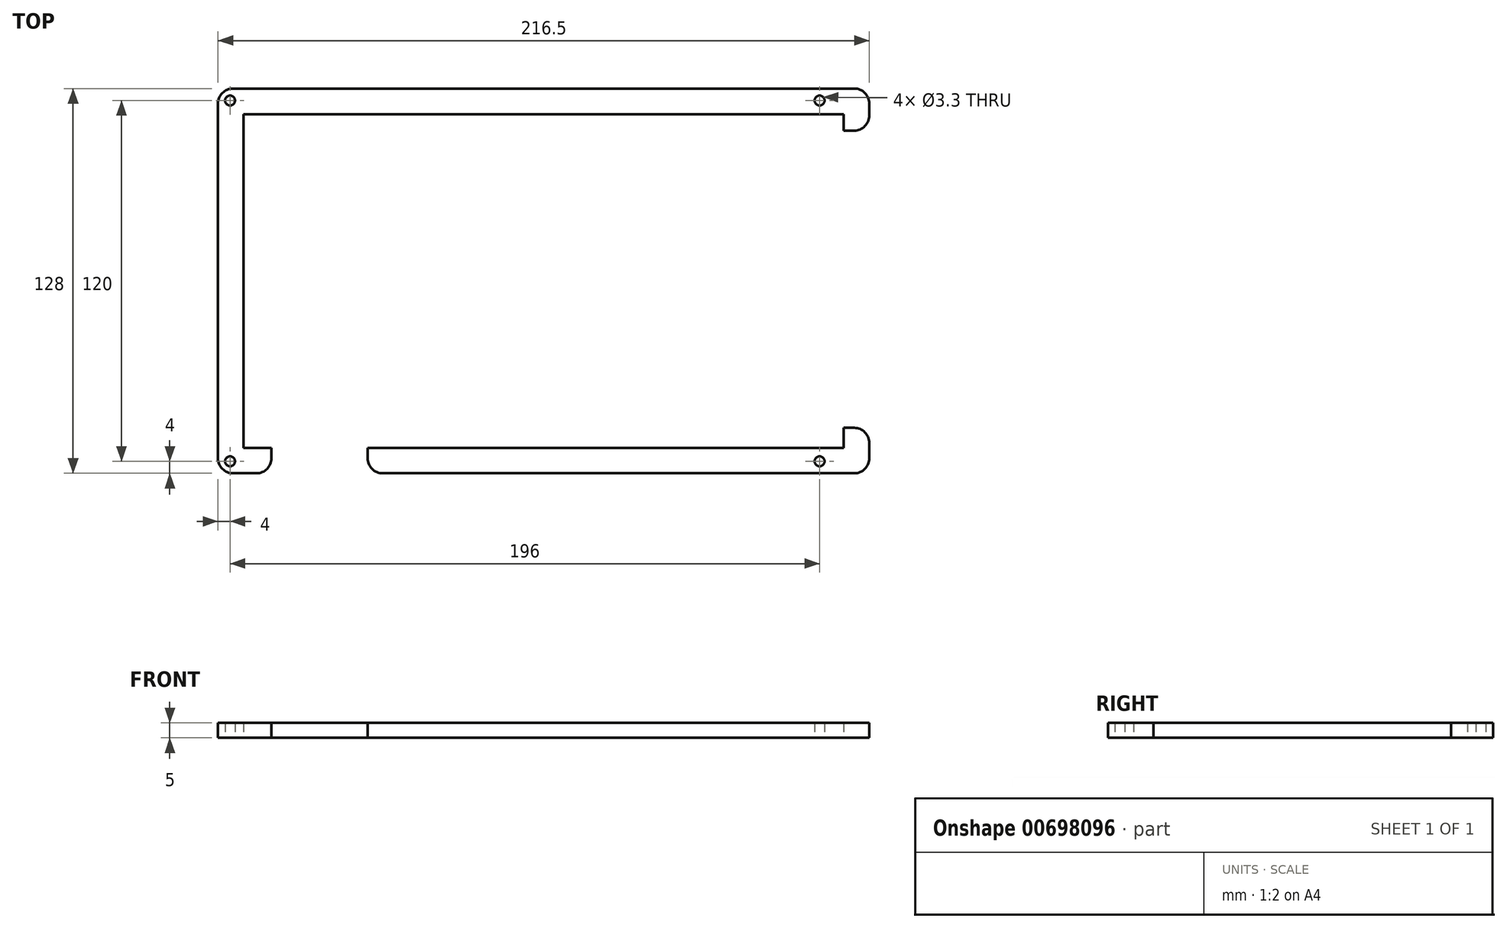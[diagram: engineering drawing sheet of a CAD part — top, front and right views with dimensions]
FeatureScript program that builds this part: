
annotation { "Feature Type Name" : "Feature", "Feature Type Description" : "" }
export const myFeature = defineFeature(function(context is Context, id is Id, definition is map)
    precondition{}
    {
        {
            var Q0;
            Q0=qCreatedBy(makeId("Top.planeOp"),FACE);
            var sketch = newSketch(context, id + "F0", { "sketchPlane" : qUnion([Q0])});
            skLineSegment(sketch, "E0.bottom", {"start": v(83, 50.5) * mm, "end": v(-57.08, 50.5) * mm});
            skLineSegment(sketch, "E0.top", {"start": v(83, -50.5) * mm, "end": v(-83, -50.5) * mm});
            skLineSegment(sketch, "E0.left", {"start": v(83, 50.5) * mm, "end": v(83, -50.5) * mm});
            skLineSegment(sketch, "E0.right", {"start": v(-83, 50.5) * mm, "end": v(-83, -50.5) * mm});
            skPoint(sketch, "E0.middle", {"position": v(0, 0) * mm});
            skLineSegment(sketch, "E1.0", {"start": v(-91, 54.5) * mm, "end": v(-91, -53.5) * mm, "construction": true});
            skLineSegment(sketch, "E1.1", {"start": v(93, 54.5) * mm, "end": v(-91, 54.5) * mm, "construction": true});
            skLineSegment(sketch, "E1.2", {"start": v(93, 54.5) * mm, "end": v(93, -53.5) * mm, "construction": true});
            skLineSegment(sketch, "E1.3", {"start": v(93, -53.5) * mm, "end": v(-91, -53.5) * mm, "construction": true});
            skLineSegment(sketch, "E2.0", {"start": v(103, 64.5) * mm, "end": v(-57.08, 64.5) * mm});
            skLineSegment(sketch, "E2.2", {"start": v(103, -63.5) * mm, "end": v(-57.08, -63.5) * mm});
            skLineSegment(sketch, "E2.3", {"start": v(-101, 64.5) * mm, "end": v(-101, -63.5) * mm});
            skLineSegment(sketch, "E3.0", {"start": v(99, 60.5) * mm, "end": v(-97, 60.5) * mm, "construction": true});
            skLineSegment(sketch, "E3.1", {"start": v(99, 60.5) * mm, "end": v(99, -59.5) * mm, "construction": true});
            skLineSegment(sketch, "E3.2", {"start": v(99, -59.5) * mm, "end": v(-97, -59.5) * mm, "construction": true});
            skLineSegment(sketch, "E3.3", {"start": v(-97, 60.5) * mm, "end": v(-97, -59.5) * mm, "construction": true});
            skLineSegment(sketch, "E4", {"start": v(103, 64.5) * mm, "end": v(115.5, 64.5) * mm});
            skLineSegment(sketch, "E5", {"start": v(115.5, -63.5) * mm, "end": v(103, -63.5) * mm});
            skLineSegment(sketch, "E6", {"start": v(115.5, 64.5) * mm, "end": v(115.5, 50.5) * mm});
            skPoint(sketch, "E7.orphan", {"position": v(133, -63.5) * mm});
            skLineSegment(sketch, "E8.0", {"start": v(103, 56) * mm, "end": v(107, 56) * mm});
            skLineSegment(sketch, "E8.1", {"start": v(-92.5, 56) * mm, "end": v(-92.5, -55) * mm});
            skLineSegment(sketch, "E8.2", {"start": v(103, -55) * mm, "end": v(-57.08, -55) * mm});
            skLineSegment(sketch, "E8.3", {"start": v(103, 56) * mm, "end": v(-57.08, 56) * mm});
            skLineSegment(sketch, "E8.4", {"start": v(107, -55) * mm, "end": v(103, -55) * mm});
            skLineSegment(sketch, "E8.5", {"start": v(107, 56) * mm, "end": v(107, 50.5) * mm});
            skLineSegment(sketch, "E9", {"start": v(-83.1, 56) * mm, "end": v(-83.07, 54.5) * mm});
            skLineSegment(sketch, "E10.trimOffspring", {"start": v(-83.24, 64.5) * mm, "end": v(-101, 64.5) * mm});
            skLineSegment(sketch, "E11.trimOffspring", {"start": v(-83.1, 56) * mm, "end": v(-92.5, 56) * mm});
            skLineSegment(sketch, "E12", {"start": v(-83.24, -63.5) * mm, "end": v(-83.24, -55) * mm});
            skLineSegment(sketch, "E13.trimOffspring", {"start": v(-57.08, 56) * mm, "end": v(-57.08, 54.5) * mm});
            skLineSegment(sketch, "E14", {"start": v(-83.24, 64.5) * mm, "end": v(-57.08, 64.5) * mm});
            skLineSegment(sketch, "E15", {"start": v(-57.08, 56) * mm, "end": v(-83.1, 56) * mm});
            skLineSegment(sketch, "E16.trimOffspring", {"start": v(-83.24, -55) * mm, "end": v(-92.5, -55) * mm});
            skLineSegment(sketch, "E17.trimOffspring", {"start": v(-83.24, -63.5) * mm, "end": v(-101, -63.5) * mm});
            skLineSegment(sketch, "E18.trimOffspring", {"start": v(-57.08, -55) * mm, "end": v(-57.08, -53.5) * mm});
            skLineSegment(sketch, "E19", {"start": v(-51.24, -63.5) * mm, "end": v(-51.24, -55) * mm});
            skLineSegment(sketch, "E20", {"start": v(107, 50.5) * mm, "end": v(115.5, 50.5) * mm});
            skLineSegment(sketch, "E21", {"start": v(107, -48.38) * mm, "end": v(115.5, -48.38) * mm});
            skLineSegment(sketch, "E22.trimOffspring", {"start": v(107, -48.38) * mm, "end": v(107, -55) * mm});
            skLineSegment(sketch, "E23.trimOffspring", {"start": v(115.5, -48.38) * mm, "end": v(115.5, -63.5) * mm});
            skSolve(sketch);
        }
        {
            var Q0;
            Q0=makeQuery(id+"F0.imprint","IMPRINT",FACE,{"disambiguationData":[TD([[makeQuery(id+"F0.imprint","IMPRINT",EDGE,{"derivedFrom":sQuery(id+"F0.wireOp",EDGE,"E2.0")}),1.0]])]});
            var Q1;
            Q1=makeQuery(id+"F0.imprint","IMPRINT",FACE,{"disambiguationData":[TD([[makeQuery(id+"F0.imprint","IMPRINT",EDGE,{"derivedFrom":sQuery(id+"F0.wireOp",EDGE,"E0.bottom")}),-1.0]])]});
            var Q2;
            {var subQ3=sQuery(id+"F0.wireOp",EDGE,"E5");Q2=makeQuery(id+"F0.imprint","IMPRINT",FACE,{"disambiguationData":[TD([[makeQuery(id+"F0.imprint","IMPRINT",EDGE,{"derivedFrom":subQ3}),-1.0]])]});}
            extrude(context, id + "F1", {"entities" : qUnion([Q0, Q1, Q2]), "depth" : 5 * mm, "offsetDistance" : 25 * mm});
        }
        {
            var Q0;
            Q0=sQuery(id+"F0.wireOp",VERTEX,"E3.0.end");
            var Q1;
            Q1=sQuery(id+"F0.wireOp",VERTEX,"E3.0.start");
            var Q2;
            Q2=sQuery(id+"F0.wireOp",VERTEX,"E3.2.end");
            var Q3;
            Q3=sQuery(id+"F0.wireOp",VERTEX,"E3.1.end");
            var Q4;
            Q4=makeQuery(id+"F1.opExtrude","SWEPT_BODY",BODY,{"disambiguationData":[OSD([sQuery(id+"F0.wireOp",EDGE,"E0.bottom"),sQuery(id+"F0.wireOp",EDGE,"E0.top"),sQuery(id+"F0.wireOp",EDGE,"E0.left"),sQuery(id+"F0.wireOp",EDGE,"E0.right"),sQuery(id+"F0.wireOp",EDGE,"E2.0"),sQuery(id+"F0.wireOp",EDGE,"E2.1"),sQuery(id+"F0.wireOp",EDGE,"E2.2"),sQuery(id+"F0.wireOp",EDGE,"E2.3")])]});
            var Q5;
            Q5=makeQuery(id+"F1.opExtrude","SWEPT_BODY",BODY,{"disambiguationData":[OSD([sQuery(id+"F0.wireOp",EDGE,"E2.2"),sQuery(id+"F0.wireOp",EDGE,"E5"),sQuery(id+"F0.wireOp",EDGE,"E8.2"),sQuery(id+"F0.wireOp",EDGE,"E8.4"),sQuery(id+"F0.wireOp",EDGE,"E19"),sQuery(id+"F0.wireOp",EDGE,"E21"),sQuery(id+"F0.wireOp",EDGE,"E22.trimOffspring"),sQuery(id+"F0.wireOp",EDGE,"E23.trimOffspring")])]});
            hole(context, id + "F2", {"style" : HoleStyle.SIMPLE, "endStyle" : HoleEndStyle.THROUGH, "oppositeDirection" : true, "standardTappedOrClearance" : lookupTablePath({ "standard" : "ISO", "fit" : "Normal", "size" : "M3", "type" : "Clearance" }), "standardBlindInLast" : lookupTablePath({ "fit" : "Standard", "standard" : "ISO", "size" : "M3", "type" : "Clearance" }), "holeDiameter" : 3.3 * mm, "majorDiameter" : 5 * mm, "isTappedThrough" : true, "tappedDepth" : 12 * mm, "tapClearance" : 3, "startFromSketch" : true, "locations" : qUnion([Q0, Q1, Q2, Q3]), "scope" : qUnion([Q4, Q5])});
        }
        {
            var Q0;
            Q0=makeQuery(id+"F1.opExtrude","SWEPT_EDGE",EDGE,{"disambiguationData":[OSD([sQuery(id+"F0.wireOp",EDGE,"E2.3"),sQuery(id+"F0.wireOp",EDGE,"E10.trimOffspring")])]});
            var Q1;
            Q1=makeQuery(id+"F1.opExtrude","SWEPT_EDGE",EDGE,{"disambiguationData":[OSD([sQuery(id+"F0.wireOp",EDGE,"E4"),sQuery(id+"F0.wireOp",EDGE,"E6")])]});
            var Q2;
            Q2=makeQuery(id+"F1.opExtrude","SWEPT_EDGE",EDGE,{"disambiguationData":[OSD([sQuery(id+"F0.wireOp",EDGE,"E5"),sQuery(id+"F0.wireOp",EDGE,"E6")])]});
            var Q3;
            Q3=makeQuery(id+"F1.opExtrude","SWEPT_EDGE",EDGE,{"disambiguationData":[OSD([sQuery(id+"F0.wireOp",EDGE,"E2.2"),sQuery(id+"F0.wireOp",EDGE,"E19")])]});
            var Q4;
            Q4=makeQuery(id+"F1.opExtrude","SWEPT_EDGE",EDGE,{"disambiguationData":[OSD([sQuery(id+"F0.wireOp",EDGE,"E2.3"),sQuery(id+"F0.wireOp",EDGE,"E17.trimOffspring")])]});
            var Q5;
            Q5=makeQuery(id+"F1.opExtrude","SWEPT_EDGE",EDGE,{"disambiguationData":[OSD([sQuery(id+"F0.wireOp",EDGE,"E12"),sQuery(id+"F0.wireOp",EDGE,"E17.trimOffspring")])]});
            fillet(context, id + "F3", {"entities" : qUnion([Q0, Q1, Q2, Q3, Q4, Q5]), "radius" : 5 * mm, "tangentPropagation" : true, "allowEdgeOverflow" : false});
        }
        {
            var Q0;
            Q0=makeQuery(id+"F1.opExtrude","SWEPT_EDGE",EDGE,{"disambiguationData":[OSD([sQuery(id+"F0.wireOp",EDGE,"E21"),sQuery(id+"F0.wireOp",EDGE,"E23.trimOffspring")])]});
            fillet(context, id + "F4", {"entities" : qUnion([Q0]), "radius" : 5 * mm, "tangentPropagation" : true, "allowEdgeOverflow" : false});
        }
    });
